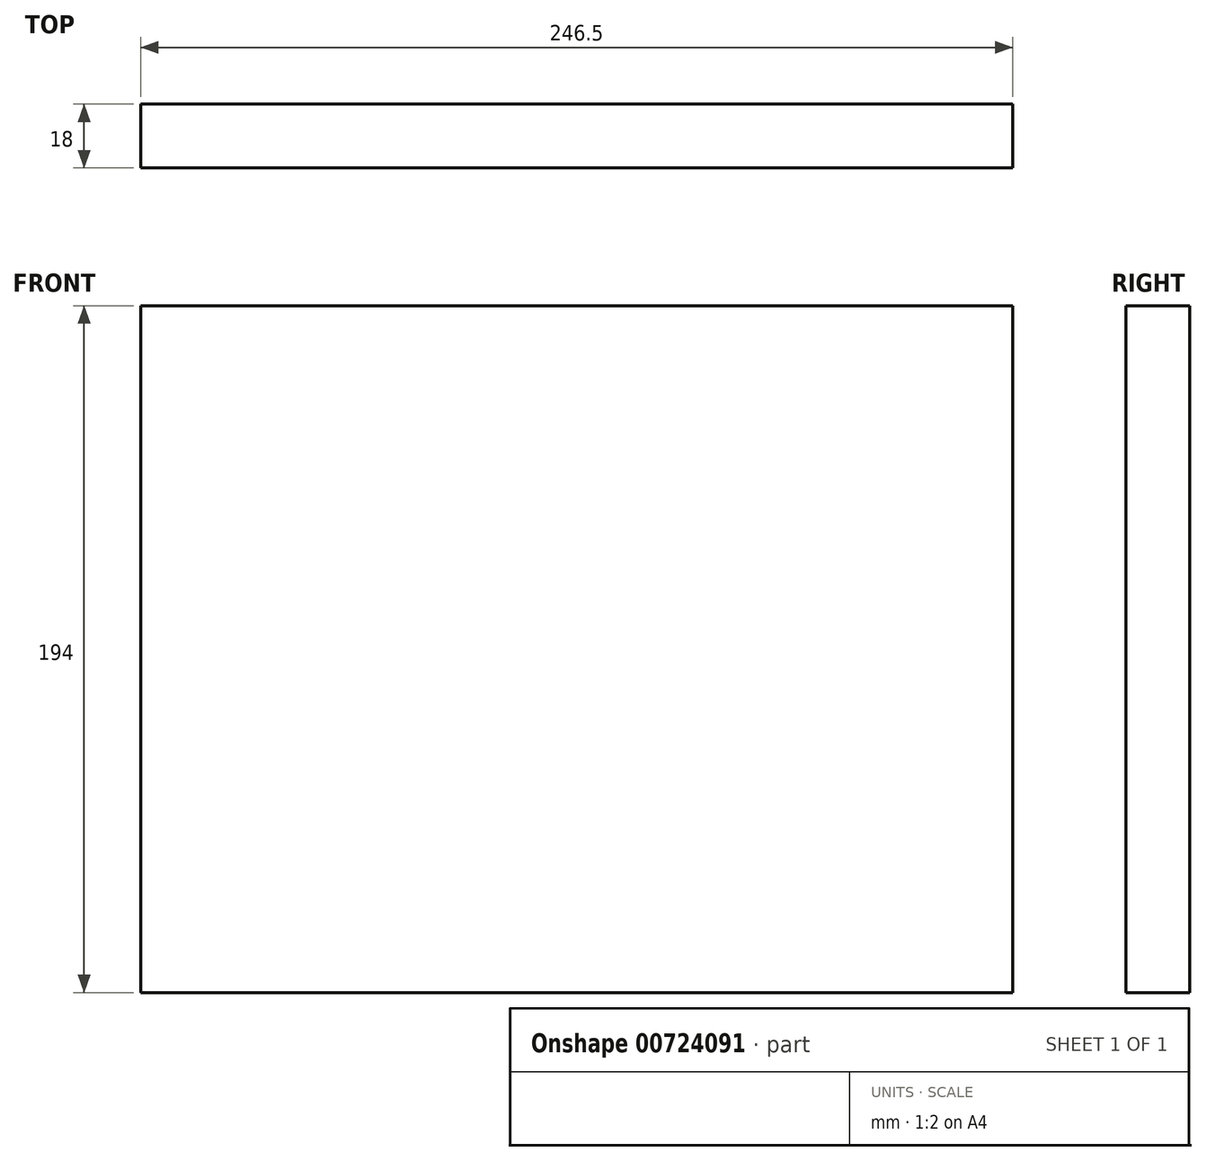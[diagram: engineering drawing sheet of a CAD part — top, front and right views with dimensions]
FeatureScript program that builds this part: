
annotation { "Feature Type Name" : "Feature", "Feature Type Description" : "" }
export const myFeature = defineFeature(function(context is Context, id is Id, definition is map)
    precondition{}
    {
        {
            var Q0;
            Q0=qCreatedBy(makeId("Front.planeOp"),FACE);
            var sketch = newSketch(context, id + "F0", { "sketchPlane" : qUnion([Q0])});
            skLineSegment(sketch, "E0.bottom", {"start": v(-123.25, 97) * mm, "end": v(123.25, 97) * mm});
            skLineSegment(sketch, "E0.top", {"start": v(-123.25, -97) * mm, "end": v(123.25, -97) * mm});
            skLineSegment(sketch, "E0.left", {"start": v(-123.25, 97) * mm, "end": v(-123.25, -97) * mm});
            skLineSegment(sketch, "E0.right", {"start": v(123.25, 97) * mm, "end": v(123.25, -97) * mm});
            skLineSegment(sketch, "E1", {"start": v(-123.25, 97) * mm, "end": v(123.25, -97) * mm, "construction": true});
            skLineSegment(sketch, "E2", {"start": v(123.25, 97) * mm, "end": v(-123.25, -97) * mm, "construction": true});
            skSolve(sketch);
        }
        {
            var Q0;
            Q0=qSketchRegion(id+"F0",true);
            extrude(context, id + "F1", {"entities" : qUnion([Q0]), "depth" : 18 * mm, "offsetDistance" : 25 * mm});
        }
    });
